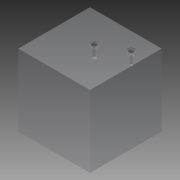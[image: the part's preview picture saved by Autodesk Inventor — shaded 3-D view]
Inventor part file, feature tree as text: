
AUTODESK INVENTOR PART (.ipt)
format: ipt  version: 2014 (Build 180170000, 170)  size: 203,776 bytes
history: native  units: mm
features: other x51, sketch x6, extrude x4
ambient origin geometry x8: Origin, YZ Plane, XZ Plane, XY Plane, X Axis, Y Axis, Z Axis, Center Point
bodies: 实体1 (feature_tree)
feature tree (61):
  extrude  "拉伸1"  TaperAngle=0.0deg  [1 undecoded]
  other  "UCS1"
  other  "UCS2"
  other  "UCS3"
  other  "UCS4"
  other  "UCS5"
  other  "UCS6"
  sketch  "草图1"  dims[d0=300.0mm d1=0.0mm]
  sketch  "草图3"  dims[d8=0.0mm d9=0.0mm d10=0.0mm d11=0.0mm d12=0.0mm d13=0.0mm]
  other  "曲面1"
  sketch  "草图4"  dims[d14=0.0mm d15=0.0mm d16=0.0mm d17=0.0mm d18=0.0mm d19=0.0mm]
  other  "曲面2"
  sketch  "草图6"  dims[d26=0.0mm d27=0.0mm d28=0.0mm d29=0.0mm d30=0.0mm d31=0.0mm d32=0.0mm d33=0.0mm d34=0.0mm d35=0.0mm d36=0.0mm d37=0.0mm d38=0.0mm d42=-31.29mm d43=0.13mm d44=0.0mm d45=-17.79mm d46=5.0mm d47=0.0mm d48=0.0mm d52=-13.99mm d53=0.13mm d54=0.0mm]
  other  "曲面3"
  extrude  "拉伸曲面1"  [1 undecoded]
  extrude  "拉伸曲面2"  Depth=5.0mm TaperAngle=0.0deg
  extrude  "拉伸曲面3"  [1 undecoded]
  other  "UCS1: YZ 平面"
  other  "UCS1: XZ 平面"
  other  "UCS1: XY 平面"
  other  "UCS1: X 轴"
  other  "UCS1: Y 轴"
  other  "UCS1: Z 轴"
  other  "UCS1: 原点"
  other  "UCS2: YZ 平面"
  other  "UCS2: XZ 平面"
  other  "UCS2: XY 平面"
  other  "UCS2: X 轴"
  other  "UCS2: Y 轴"
  other  "UCS2: Z 轴"
  other  "UCS2: 原点"
  other  "UCS3: YZ 平面"
  other  "UCS3: XZ 平面"
  other  "UCS3: XY 平面"
  other  "UCS3: X 轴"
  other  "UCS3: Y 轴"
  other  "UCS3: Z 轴"
  other  "UCS3: 原点"
  other  "UCS4: YZ 平面"
  other  "UCS4: XZ 平面"
  other  "UCS4: XY 平面"
  other  "UCS4: X 轴"
  other  "UCS4: Y 轴"
  other  "UCS4: Z 轴"
  other  "UCS4: 原点"
  other  "UCS5: YZ 平面"
  other  "UCS5: XZ 平面"
  other  "UCS5: XY 平面"
  other  "UCS5: X 轴"
  other  "UCS5: Y 轴"
  other  "UCS5: Z 轴"
  other  "UCS5: 原点"
  other  "UCS6: YZ 平面"
  other  "UCS6: XZ 平面"
  other  "UCS6: XY 平面"
  other  "UCS6: X 轴"
  other  "UCS6: Y 轴"
  other  "UCS6: Z 轴"
  other  "UCS6: 原点"
  sketch  "草图2"  dims[d2=0.0mm d3=0.0mm d4=0.0mm d5=0.0mm d6=0.0mm d7=0.0mm]
  sketch  "草图5"  dims[d20=0.0mm d21=0.0mm d22=0.0mm d23=0.0mm d24=0.0mm d25=0.0mm]
note: 3 required parameter values undecoded (feature->parameter linkage not recoverable at this tier; creation-order binding heuristic only, values carry confidence <= 0.55)
